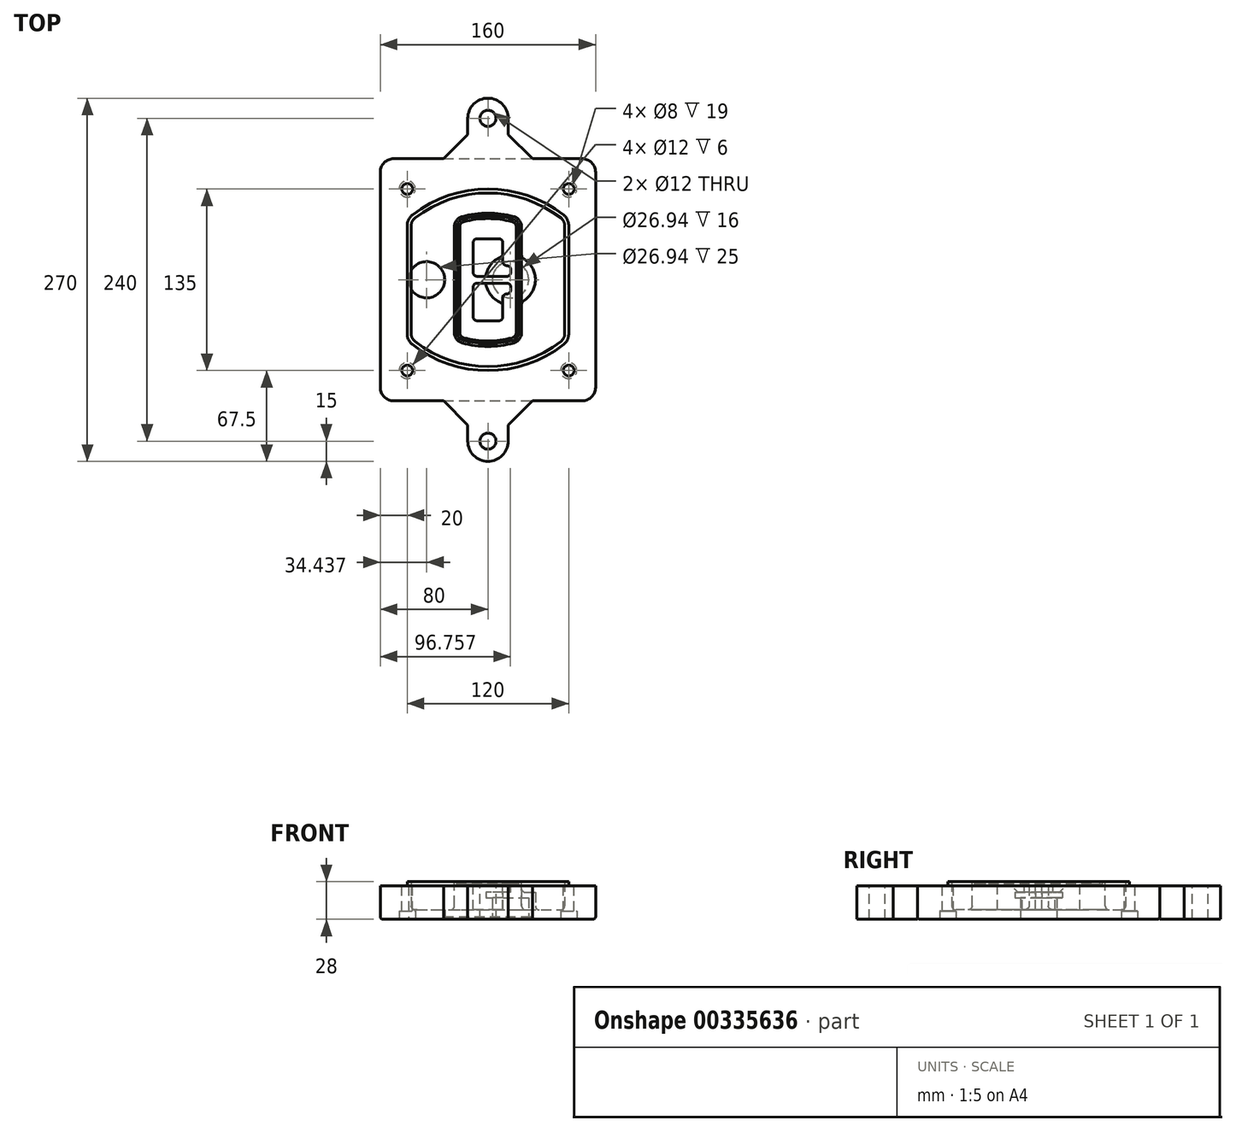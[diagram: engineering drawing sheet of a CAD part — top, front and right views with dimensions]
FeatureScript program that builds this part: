
annotation { "Feature Type Name" : "Feature", "Feature Type Description" : "" }
export const myFeature = defineFeature(function(context is Context, id is Id, definition is map)
    precondition{}
    {
        {
            var Q0;
            Q0=qCreatedBy(makeId("Top.planeOp"),FACE);
            var sketch = newSketch(context, id + "F0", { "sketchPlane" : qUnion([Q0])});
            skPoint(sketch, "E0.rect.middle", {"position": v(0, 0) * mm});
            skLineSegment(sketch, "E1.bottom", {"start": v(-70, -90) * mm, "end": v(70, -90) * mm});
            skLineSegment(sketch, "E1.top", {"start": v(-70, 90) * mm, "end": v(70, 90) * mm});
            skLineSegment(sketch, "E1.left", {"start": v(-80, -80) * mm, "end": v(-80, 80) * mm});
            skLineSegment(sketch, "E1.right", {"start": v(80, -80) * mm, "end": v(80, 80) * mm});
            skLineSegment(sketch, "E2", {"start": v(-80, 90) * mm, "end": v(80, -90) * mm, "construction": true});
            skLineSegment(sketch, "E3", {"start": v(80, 90) * mm, "end": v(-80, -90) * mm, "construction": true});
            skCircle(sketch, "E4", {"center": v(-60, 67.5) * mm, "radius": 4 * mm});
            skCircle(sketch, "E5", {"center": v(60, 67.5) * mm, "radius": 4 * mm});
            skCircle(sketch, "E6", {"center": v(60, -67.5) * mm, "radius": 4 * mm});
            skCircle(sketch, "E7", {"center": v(-60, -67.5) * mm, "radius": 4 * mm});
            skLineSegment(sketch, "E8", {"start": v(-60, 67.5) * mm, "end": v(60, 67.5) * mm, "construction": true});
            skLineSegment(sketch, "E9", {"start": v(60, 67.5) * mm, "end": v(60, -67.5) * mm, "construction": true});
            skLineSegment(sketch, "E10", {"start": v(60, -67.5) * mm, "end": v(-60, -67.5) * mm, "construction": true});
            skLineSegment(sketch, "E11", {"start": v(-60, -67.5) * mm, "end": v(-60, 67.5) * mm, "construction": true});
            skLineSegment(sketch, "E12", {"start": v(-60, 40.3) * mm, "end": v(-60, -40.3) * mm});
            skLineSegment(sketch, "E13", {"start": v(60, 40.3) * mm, "end": v(60, -40.3) * mm});
            skArc(sketch, "E14", {"start": v(56.15, 48.18) * mm, "mid": v(0, 67.5) * mm, "end": v(-56.15, 48.18) * mm});
            skArc(sketch, "E15", {"start": v(-56.15, -48.18) * mm, "mid": v(0, -67.5) * mm, "end": v(56.15, -48.18) * mm});
            skLineSegment(sketch, "E16", {"start": v(-60, 0) * mm, "end": v(60, 0) * mm, "construction": true});
            skPoint(sketch, "E17.visualSharp", {"position": v(-60, -45) * mm});
            skArc(sketch, "E17.filletArc", {"start": v(-60, -40.3) * mm, "mid": v(-58.99, -44.68) * mm, "end": v(-56.15, -48.18) * mm});
            skPoint(sketch, "E18.visualSharp", {"position": v(-60, 45) * mm});
            skArc(sketch, "E18.filletArc", {"start": v(-56.15, 48.18) * mm, "mid": v(-58.99, 44.68) * mm, "end": v(-60, 40.3) * mm});
            skPoint(sketch, "E19.visualSharp", {"position": v(60, 45) * mm});
            skArc(sketch, "E19.filletArc", {"start": v(60, 40.3) * mm, "mid": v(58.99, 44.68) * mm, "end": v(56.15, 48.18) * mm});
            skPoint(sketch, "E20.visualSharp", {"position": v(60, -45) * mm});
            skArc(sketch, "E20.filletArc", {"start": v(56.15, -48.18) * mm, "mid": v(58.99, -44.68) * mm, "end": v(60, -40.3) * mm});
            skPoint(sketch, "E21.visualSharp", {"position": v(-80, 90) * mm});
            skArc(sketch, "E21.filletArc", {"start": v(-70, 90) * mm, "mid": v(-77.07, 87.07) * mm, "end": v(-80, 80) * mm});
            skPoint(sketch, "E22.visualSharp", {"position": v(80, 90) * mm});
            skArc(sketch, "E22.filletArc", {"start": v(80, 80) * mm, "mid": v(77.07, 87.07) * mm, "end": v(70, 90) * mm});
            skPoint(sketch, "E23.visualSharp", {"position": v(80, -90) * mm});
            skArc(sketch, "E23.filletArc", {"start": v(70, -90) * mm, "mid": v(77.07, -87.07) * mm, "end": v(80, -80) * mm});
            skPoint(sketch, "E24.visualSharp", {"position": v(-80, -90) * mm});
            skArc(sketch, "E24.filletArc", {"start": v(-80, -80) * mm, "mid": v(-77.07, -87.07) * mm, "end": v(-70, -90) * mm});
            skArc(sketch, "E25.0", {"start": v(57, 40.3) * mm, "mid": v(56.3, 43.36) * mm, "end": v(54.3, 45.81) * mm});
            skLineSegment(sketch, "E25.1", {"start": v(57, 40.3) * mm, "end": v(57, -40.3) * mm});
            skArc(sketch, "E25.2", {"start": v(54.3, -45.81) * mm, "mid": v(56.3, -43.36) * mm, "end": v(57, -40.3) * mm});
            skArc(sketch, "E25.3", {"start": v(-54.3, -45.81) * mm, "mid": v(0, -64.5) * mm, "end": v(54.3, -45.81) * mm});
            skArc(sketch, "E25.4", {"start": v(-57, -40.3) * mm, "mid": v(-56.3, -43.36) * mm, "end": v(-54.3, -45.81) * mm});
            skArc(sketch, "E25.5", {"start": v(54.3, 45.81) * mm, "mid": v(0, 64.5) * mm, "end": v(-54.3, 45.81) * mm});
            skLineSegment(sketch, "E25.6", {"start": v(-57, 40.3) * mm, "end": v(-57, -40.3) * mm});
            skArc(sketch, "E25.7", {"start": v(-54.3, 45.81) * mm, "mid": v(-56.3, 43.36) * mm, "end": v(-57, 40.3) * mm});
            skArc(sketch, "E26.0", {"start": v(-58.62, 51.33) * mm, "mid": v(-62.58, 46.43) * mm, "end": v(-64, 40.3) * mm});
            skArc(sketch, "E26.1", {"start": v(58.62, 51.33) * mm, "mid": v(0, 71.5) * mm, "end": v(-58.62, 51.33) * mm});
            skArc(sketch, "E26.2", {"start": v(64, 40.3) * mm, "mid": v(62.58, 46.43) * mm, "end": v(58.62, 51.33) * mm});
            skLineSegment(sketch, "E26.3", {"start": v(64, 40.3) * mm, "end": v(64, -40.3) * mm});
            skArc(sketch, "E26.4", {"start": v(58.62, -51.33) * mm, "mid": v(62.58, -46.43) * mm, "end": v(64, -40.3) * mm});
            skLineSegment(sketch, "E26.5", {"start": v(-64, 40.3) * mm, "end": v(-64, -40.3) * mm});
            skArc(sketch, "E26.6", {"start": v(-58.62, -51.33) * mm, "mid": v(0, -71.5) * mm, "end": v(58.62, -51.33) * mm});
            skArc(sketch, "E26.7", {"start": v(-64, -40.3) * mm, "mid": v(-62.58, -46.43) * mm, "end": v(-58.62, -51.33) * mm});
            skSolve(sketch);
        }
        {
            var Q0;
            Q0=makeQuery(id+"F0.imprint","IMPRINT",FACE,{"disambiguationData":[TD([[makeQuery(id+"F0.imprint","IMPRINT",EDGE,{"derivedFrom":sQuery(id+"F0.wireOp",EDGE,"E1.bottom")}),1.0]])]});
            var Q1;
            Q1=makeQuery(id+"F0.imprint","IMPRINT",FACE,{"disambiguationData":[TD([[makeQuery(id+"F0.imprint","IMPRINT",EDGE,{"derivedFrom":sQuery(id+"F0.wireOp",EDGE,"E12")}),1.0]])]});
            var Q2;
            Q2=makeQuery(id+"F0.imprint","IMPRINT",FACE,{"disambiguationData":[TD([[makeQuery(id+"F0.imprint","IMPRINT",EDGE,{"derivedFrom":sQuery(id+"F0.wireOp",EDGE,"E25.0")}),1.0]])]});
            var Q3;
            Q3=makeQuery(id+"F0.imprint","IMPRINT",FACE,{"disambiguationData":[TD([[makeQuery(id+"F0.imprint","IMPRINT",EDGE,{"derivedFrom":sQuery(id+"F0.wireOp",EDGE,"E12")}),-1.0]])]});
            extrude(context, id + "F1", {"entities" : qUnion([Q0, Q1, Q2, Q3]), "oppositeDirection" : true, "depth" : 25 * mm});
        }
        {
            var Q0;
            Q0=makeQuery(id+"F0.imprint","IMPRINT",FACE,{"disambiguationData":[TD([[makeQuery(id+"F0.imprint","IMPRINT",EDGE,{"derivedFrom":sQuery(id+"F0.wireOp",EDGE,"E12")}),1.0]])]});
            extrude(context, id + "F2", {"entities" : qUnion([Q0]), "operationType" : NewBodyOperationType.ADD, "depth" : 3 * mm});
        }
        {
            var Q0;
            Q0=makeQuery(id+"F0.imprint","IMPRINT",FACE,{"disambiguationData":[TD([[makeQuery(id+"F0.imprint","IMPRINT",EDGE,{"derivedFrom":sQuery(id+"F0.wireOp",EDGE,"E25.0")}),1.0]])]});
            extrude(context, id + "F3", {"entities" : qUnion([Q0]), "operationType" : NewBodyOperationType.REMOVE, "oppositeDirection" : true, "depth" : 18 * mm});
        }
        {
            var Q0;
            Q0=makeQuery(id+"F2.opExtrude","CAP_FACE",FACE,{"disambiguationData":[OSD([sQuery(id+"F0.wireOp",EDGE,"E12"),sQuery(id+"F0.wireOp",EDGE,"E13"),sQuery(id+"F0.wireOp",EDGE,"E14"),sQuery(id+"F0.wireOp",EDGE,"E15"),sQuery(id+"F0.wireOp",EDGE,"E17.filletArc"),sQuery(id+"F0.wireOp",EDGE,"E18.filletArc"),sQuery(id+"F0.wireOp",EDGE,"E19.filletArc"),sQuery(id+"F0.wireOp",EDGE,"E20.filletArc"),sQuery(id+"F0.wireOp",EDGE,"E25.0"),sQuery(id+"F0.wireOp",EDGE,"E25.1"),sQuery(id+"F0.wireOp",EDGE,"E25.2"),sQuery(id+"F0.wireOp",EDGE,"E25.3"),sQuery(id+"F0.wireOp",EDGE,"E25.4"),sQuery(id+"F0.wireOp",EDGE,"E25.5"),sQuery(id+"F0.wireOp",EDGE,"E25.6"),sQuery(id+"F0.wireOp",EDGE,"E25.7")])],"isStart":false});
            var sketch = newSketch(context, id + "F4", { "sketchPlane" : qUnion([Q0])});
            skArc(sketch, "E27.0", {"start": v(-19.08, -46.97) * mm, "mid": v(0, -49.5) * mm, "end": v(19.08, -46.97) * mm});
            skArc(sketch, "E28.0", {"start": v(19.08, 46.97) * mm, "mid": v(0, 49.5) * mm, "end": v(-19.08, 46.97) * mm});
            skLineSegment(sketch, "E29", {"start": v(-25, 39.25) * mm, "end": v(-25, -39.25) * mm});
            skLineSegment(sketch, "E30", {"start": v(25, 39.25) * mm, "end": v(25, -39.25) * mm});
            skLineSegment(sketch, "E31", {"start": v(-25, 45.1) * mm, "end": v(25, 45.1) * mm, "construction": true});
            skLineSegment(sketch, "E32", {"start": v(-25, -45.1) * mm, "end": v(25, -45.1) * mm, "construction": true});
            skPoint(sketch, "E33.visualSharp", {"position": v(-25, 45.1) * mm});
            skArc(sketch, "E33.filletArc", {"start": v(-19.08, 46.97) * mm, "mid": v(-23.35, 44.11) * mm, "end": v(-25, 39.25) * mm});
            skPoint(sketch, "E34.visualSharp", {"position": v(25, 45.1) * mm});
            skArc(sketch, "E34.filletArc", {"start": v(25, 39.25) * mm, "mid": v(23.35, 44.11) * mm, "end": v(19.08, 46.97) * mm});
            skPoint(sketch, "E35.visualSharp", {"position": v(25, -45.1) * mm});
            skArc(sketch, "E35.filletArc", {"start": v(19.08, -46.97) * mm, "mid": v(23.35, -44.11) * mm, "end": v(25, -39.25) * mm});
            skPoint(sketch, "E36.visualSharp", {"position": v(-25, -45.1) * mm});
            skArc(sketch, "E36.filletArc", {"start": v(-25, -39.25) * mm, "mid": v(-23.35, -44.11) * mm, "end": v(-19.08, -46.97) * mm});
            skArc(sketch, "E37.0", {"start": v(54.3, 45.81) * mm, "mid": v(0, 64.5) * mm, "end": v(-54.3, 45.81) * mm});
            skArc(sketch, "E37.1", {"start": v(-54.3, 45.81) * mm, "mid": v(-56.3, 43.36) * mm, "end": v(-57, 40.3) * mm});
            skLineSegment(sketch, "E37.2", {"start": v(-57, 40.3) * mm, "end": v(-57, -40.3) * mm});
            skArc(sketch, "E37.3", {"start": v(-57, -40.3) * mm, "mid": v(-56.3, -43.36) * mm, "end": v(-54.3, -45.81) * mm});
            skArc(sketch, "E37.4", {"start": v(-54.3, -45.81) * mm, "mid": v(0, -64.5) * mm, "end": v(54.3, -45.81) * mm});
            skArc(sketch, "E37.5", {"start": v(54.3, -45.81) * mm, "mid": v(56.3, -43.36) * mm, "end": v(57, -40.3) * mm});
            skLineSegment(sketch, "E37.6", {"start": v(57, 40.3) * mm, "end": v(57, -40.3) * mm});
            skArc(sketch, "E37.7", {"start": v(57, 40.3) * mm, "mid": v(56.3, 43.36) * mm, "end": v(54.3, 45.81) * mm});
            skLineSegment(sketch, "E38.0", {"start": v(23, 39.25) * mm, "end": v(23, -39.25) * mm});
            skArc(sketch, "E38.1", {"start": v(18.56, -45.04) * mm, "mid": v(21.76, -42.9) * mm, "end": v(23, -39.25) * mm});
            skArc(sketch, "E38.2", {"start": v(-18.56, -45.04) * mm, "mid": v(0, -47.5) * mm, "end": v(18.56, -45.04) * mm});
            skArc(sketch, "E38.3", {"start": v(-23, -39.25) * mm, "mid": v(-21.76, -42.9) * mm, "end": v(-18.56, -45.04) * mm});
            skLineSegment(sketch, "E38.4", {"start": v(-23, 39.25) * mm, "end": v(-23, -39.25) * mm});
            skArc(sketch, "E38.5", {"start": v(23, 39.25) * mm, "mid": v(21.76, 42.9) * mm, "end": v(18.56, 45.04) * mm});
            skArc(sketch, "E38.6", {"start": v(-18.56, 45.04) * mm, "mid": v(-21.76, 42.9) * mm, "end": v(-23, 39.25) * mm});
            skArc(sketch, "E38.7", {"start": v(18.56, 45.04) * mm, "mid": v(0, 47.5) * mm, "end": v(-18.56, 45.04) * mm});
            skArc(sketch, "E39.0", {"start": v(21, 39.25) * mm, "mid": v(20.18, 41.68) * mm, "end": v(18.04, 43.1) * mm});
            skLineSegment(sketch, "E39.1", {"start": v(21, 39.25) * mm, "end": v(21, -39.25) * mm});
            skArc(sketch, "E39.2", {"start": v(18.04, -43.1) * mm, "mid": v(20.18, -41.68) * mm, "end": v(21, -39.25) * mm});
            skArc(sketch, "E39.3", {"start": v(-18.04, -43.1) * mm, "mid": v(0, -45.5) * mm, "end": v(18.04, -43.1) * mm});
            skArc(sketch, "E39.4", {"start": v(-21, -39.25) * mm, "mid": v(-20.18, -41.68) * mm, "end": v(-18.04, -43.1) * mm});
            skArc(sketch, "E39.5", {"start": v(18.04, 43.1) * mm, "mid": v(0, 45.5) * mm, "end": v(-18.04, 43.1) * mm});
            skLineSegment(sketch, "E39.6", {"start": v(-21, 39.25) * mm, "end": v(-21, -39.25) * mm});
            skArc(sketch, "E39.7", {"start": v(-18.04, 43.1) * mm, "mid": v(-20.18, 41.68) * mm, "end": v(-21, 39.25) * mm});
            skLineSegment(sketch, "E40", {"start": v(-25, 0) * mm, "end": v(25, 0) * mm, "construction": true});
            skLineSegment(sketch, "E41", {"start": v(-11, 5.5) * mm, "end": v(-11, 27.5) * mm});
            skLineSegment(sketch, "E42", {"start": v(-8, 30.5) * mm, "end": v(8, 30.5) * mm});
            skLineSegment(sketch, "E43", {"start": v(11, 27.5) * mm, "end": v(11, 13.5) * mm});
            skLineSegment(sketch, "E44", {"start": v(14, 10.5) * mm, "end": v(14, 10.5) * mm});
            skLineSegment(sketch, "E45", {"start": v(17, 7.5) * mm, "end": v(17, 5.5) * mm});
            skLineSegment(sketch, "E46", {"start": v(14, 2.5) * mm, "end": v(-8, 2.5) * mm});
            skPoint(sketch, "E47.visualSharp", {"position": v(-11, 30.5) * mm});
            skArc(sketch, "E47.filletArc", {"start": v(-8, 30.5) * mm, "mid": v(-10.12, 29.62) * mm, "end": v(-11, 27.5) * mm});
            skPoint(sketch, "E48.visualSharp", {"position": v(11, 30.5) * mm});
            skArc(sketch, "E48.filletArc", {"start": v(11, 27.5) * mm, "mid": v(10.12, 29.62) * mm, "end": v(8, 30.5) * mm});
            skPoint(sketch, "E49.visualSharp", {"position": v(11, 10.5) * mm});
            skArc(sketch, "E49.filletArc", {"start": v(11, 13.5) * mm, "mid": v(11.88, 11.38) * mm, "end": v(14, 10.5) * mm});
            skPoint(sketch, "E50.visualSharp", {"position": v(17, 10.5) * mm});
            skArc(sketch, "E50.filletArc", {"start": v(17, 7.5) * mm, "mid": v(16.12, 9.62) * mm, "end": v(14, 10.5) * mm});
            skPoint(sketch, "E51.visualSharp", {"position": v(17, 2.5) * mm});
            skArc(sketch, "E51.filletArc", {"start": v(14, 2.5) * mm, "mid": v(16.12, 3.38) * mm, "end": v(17, 5.5) * mm});
            skPoint(sketch, "E52.visualSharp", {"position": v(-11, 2.5) * mm});
            skArc(sketch, "E52.filletArc", {"start": v(-11, 5.5) * mm, "mid": v(-10.12, 3.38) * mm, "end": v(-8, 2.5) * mm});
            skLineSegment(sketch, "E53.0.MirrorCS", {"start": v(14, -2.5) * mm, "end": v(-8, -2.5) * mm});
            skArc(sketch, "E54.0.MirrorCS", {"start": v(-11, -5.5) * mm, "mid": v(-10.12, -3.38) * mm, "end": v(-8, -2.5) * mm});
            skLineSegment(sketch, "E55.0.MirrorCS", {"start": v(-11, -5.5) * mm, "end": v(-11, -27.5) * mm});
            skArc(sketch, "E56.0.MirrorCS", {"start": v(-8, -30.5) * mm, "mid": v(-10.12, -29.62) * mm, "end": v(-11, -27.5) * mm});
            skLineSegment(sketch, "E57.0.MirrorCS", {"start": v(-8, -30.5) * mm, "end": v(8, -30.5) * mm});
            skArc(sketch, "E58.0.MirrorCS", {"start": v(11, -27.5) * mm, "mid": v(10.12, -29.62) * mm, "end": v(8, -30.5) * mm});
            skLineSegment(sketch, "E59.0.MirrorCS", {"start": v(11, -27.5) * mm, "end": v(11, -13.5) * mm});
            skArc(sketch, "E60.0.MirrorCS", {"start": v(11, -13.5) * mm, "mid": v(11.88, -11.38) * mm, "end": v(14, -10.5) * mm});
            skArc(sketch, "E61.0.MirrorCS", {"start": v(17, -7.5) * mm, "mid": v(16.12, -9.62) * mm, "end": v(14, -10.5) * mm});
            skLineSegment(sketch, "E62.0.MirrorCS", {"start": v(17, -7.5) * mm, "end": v(17, -5.5) * mm});
            skArc(sketch, "E63.0.MirrorCS", {"start": v(14, -2.5) * mm, "mid": v(16.12, -3.38) * mm, "end": v(17, -5.5) * mm});
            skSolve(sketch);
        }
        {
            var Q0;
            Q0=makeQuery(id+"F4.imprint","IMPRINT",FACE,{"disambiguationData":[TD([[makeQuery(id+"F4.imprint","IMPRINT",EDGE,{"derivedFrom":sQuery(id+"F4.wireOp",EDGE,"E27.0")}),1.0]])]});
            var Q1;
            Q1=makeQuery(id+"F4.imprint","IMPRINT",FACE,{"disambiguationData":[TD([[makeQuery(id+"F4.imprint","IMPRINT",EDGE,{"derivedFrom":sQuery(id+"F4.wireOp",EDGE,"E38.0")}),-1.0]])]});
            var Q2;
            Q2=makeQuery(id+"F4.imprint","IMPRINT",FACE,{"disambiguationData":[TD([[makeQuery(id+"F4.imprint","IMPRINT",EDGE,{"derivedFrom":sQuery(id+"F4.wireOp",EDGE,"E39.0")}),1.0]])]});
            extrude(context, id + "F5", {"entities" : qUnion([Q0, Q1, Q2]), "operationType" : NewBodyOperationType.ADD, "endBound" : BoundingType.UP_TO_NEXT, "oppositeDirection" : true, "depth" : 25 * mm});
        }
        {
            var Q0;
            Q0=makeQuery(id+"F4.imprint","IMPRINT",FACE,{"disambiguationData":[TD([[makeQuery(id+"F4.imprint","IMPRINT",EDGE,{"derivedFrom":sQuery(id+"F4.wireOp",EDGE,"E38.0")}),-1.0]])]});
            extrude(context, id + "F6", {"entities" : qUnion([Q0]), "operationType" : NewBodyOperationType.REMOVE, "oppositeDirection" : true, "depth" : 2 * mm});
        }
        {
            var Q0;
            Q0=makeQuery(id+"F1.opExtrude","CAP_FACE",FACE,{"disambiguationData":[OSD([sQuery(id+"F0.wireOp",EDGE,"E1.bottom"),sQuery(id+"F0.wireOp",EDGE,"E1.top"),sQuery(id+"F0.wireOp",EDGE,"E1.left"),sQuery(id+"F0.wireOp",EDGE,"E1.right"),sQuery(id+"F0.wireOp",EDGE,"E4"),sQuery(id+"F0.wireOp",EDGE,"E5"),sQuery(id+"F0.wireOp",EDGE,"E6"),sQuery(id+"F0.wireOp",EDGE,"E7"),sQuery(id+"F0.wireOp",EDGE,"E21.filletArc"),sQuery(id+"F0.wireOp",EDGE,"E22.filletArc"),sQuery(id+"F0.wireOp",EDGE,"E23.filletArc"),sQuery(id+"F0.wireOp",EDGE,"E24.filletArc")])],"isStart":false});
            var sketch = newSketch(context, id + "F7", { "sketchPlane" : qUnion([Q0])});
            skCircle(sketch, "E64", {"center": v(16.76, 0) * mm, "radius": 13.47 * mm});
            skCircle(sketch, "E65", {"center": v(-45.56, 0) * mm, "radius": 13.47 * mm});
            skLineSegment(sketch, "E66", {"start": v(80, 0) * mm, "end": v(-80, 0) * mm});
            skCircle(sketch, "E67", {"center": v(16.76, 0) * mm, "radius": 18.47 * mm});
            skCircle(sketch, "E68", {"center": v(60, -67.5) * mm, "radius": 6 * mm});
            skCircle(sketch, "E69", {"center": v(-60, -67.5) * mm, "radius": 6 * mm});
            skCircle(sketch, "E70", {"center": v(-60, 67.5) * mm, "radius": 6 * mm});
            skCircle(sketch, "E71", {"center": v(60, 67.5) * mm, "radius": 6 * mm});
            skSolve(sketch);
        }
        {
            var Q0;
            {var subQ1=sQuery(id+"F7.wireOp",EDGE,"E66");var subQ4=sQuery(id+"F7.wireOp",EDGE,"E64");var subQ6=makeQuery(id+"F7.imprint","INTERSECT",VERTEX,{"disambiguationData":[OD(0.0)],"derivedFrom":[subQ4,subQ1]});Q0=makeQuery(id+"F7.imprint","IMPRINT",FACE,{"disambiguationData":[TD([[makeQuery(id+"F7.imprint","IMPRINT",EDGE,{"disambiguationData":[TD([[subQ6,-1.0]])],"derivedFrom":subQ4}),-1.0]])]});}
            var Q1;
            {var subQ0=sQuery(id+"F7.wireOp",EDGE,"E66");var subQ1=sQuery(id+"F7.wireOp",EDGE,"E64");var subQ3=makeQuery(id+"F7.imprint","INTERSECT",VERTEX,{"disambiguationData":[OD(0.0)],"derivedFrom":[subQ1,subQ0]});Q1=makeQuery(id+"F7.imprint","IMPRINT",FACE,{"disambiguationData":[TD([[makeQuery(id+"F7.imprint","IMPRINT",EDGE,{"disambiguationData":[TD([[subQ3,-1.0]])],"derivedFrom":subQ1}),1.0]])]});}
            var Q2;
            {var subQ0=sQuery(id+"F7.wireOp",EDGE,"E66");var subQ1=sQuery(id+"F7.wireOp",EDGE,"E64");var subQ3=makeQuery(id+"F7.imprint","INTERSECT",VERTEX,{"disambiguationData":[OD(0.0)],"derivedFrom":[subQ1,subQ0]});Q2=makeQuery(id+"F7.imprint","IMPRINT",FACE,{"disambiguationData":[TD([[makeQuery(id+"F7.imprint","IMPRINT",EDGE,{"disambiguationData":[TD([[subQ3,1.0]])],"derivedFrom":subQ1}),1.0]])]});}
            var Q3;
            {var subQ1=sQuery(id+"F7.wireOp",EDGE,"E66");var subQ4=sQuery(id+"F7.wireOp",EDGE,"E64");var subQ6=makeQuery(id+"F7.imprint","INTERSECT",VERTEX,{"disambiguationData":[OD(0.0)],"derivedFrom":[subQ4,subQ1]});Q3=makeQuery(id+"F7.imprint","IMPRINT",FACE,{"disambiguationData":[TD([[makeQuery(id+"F7.imprint","IMPRINT",EDGE,{"disambiguationData":[TD([[subQ6,1.0]])],"derivedFrom":subQ4}),-1.0]])]});}
            extrude(context, id + "F8", {"entities" : qUnion([Q0, Q1, Q2, Q3]), "operationType" : NewBodyOperationType.ADD, "oppositeDirection" : true, "depth" : 20 * mm});
        }
        {
            var Q0;
            {var subQ0=sQuery(id+"F7.wireOp",EDGE,"E66");var subQ1=sQuery(id+"F7.wireOp",EDGE,"E64");var subQ3=makeQuery(id+"F7.imprint","INTERSECT",VERTEX,{"disambiguationData":[OD(0.0)],"derivedFrom":[subQ1,subQ0]});Q0=makeQuery(id+"F7.imprint","IMPRINT",FACE,{"disambiguationData":[TD([[makeQuery(id+"F7.imprint","IMPRINT",EDGE,{"disambiguationData":[TD([[subQ3,-1.0]])],"derivedFrom":subQ1}),1.0]])]});}
            var Q1;
            {var subQ0=sQuery(id+"F7.wireOp",EDGE,"E66");var subQ1=sQuery(id+"F7.wireOp",EDGE,"E64");var subQ3=makeQuery(id+"F7.imprint","INTERSECT",VERTEX,{"disambiguationData":[OD(0.0)],"derivedFrom":[subQ1,subQ0]});Q1=makeQuery(id+"F7.imprint","IMPRINT",FACE,{"disambiguationData":[TD([[makeQuery(id+"F7.imprint","IMPRINT",EDGE,{"disambiguationData":[TD([[subQ3,1.0]])],"derivedFrom":subQ1}),1.0]])]});}
            extrude(context, id + "F9", {"entities" : qUnion([Q0, Q1]), "operationType" : NewBodyOperationType.REMOVE, "oppositeDirection" : true, "depth" : 16 * mm});
        }
        {
            var Q0;
            {var subQ0=sQuery(id+"F7.wireOp",EDGE,"E66");var subQ1=sQuery(id+"F7.wireOp",EDGE,"E65");var subQ3=makeQuery(id+"F7.imprint","INTERSECT",VERTEX,{"disambiguationData":[OD(0.0)],"derivedFrom":[subQ1,subQ0]});Q0=makeQuery(id+"F7.imprint","IMPRINT",FACE,{"disambiguationData":[TD([[makeQuery(id+"F7.imprint","IMPRINT",EDGE,{"disambiguationData":[TD([[subQ3,-1.0]])],"derivedFrom":subQ1}),1.0]])]});}
            var Q1;
            {var subQ0=sQuery(id+"F7.wireOp",EDGE,"E66");var subQ1=sQuery(id+"F7.wireOp",EDGE,"E65");var subQ3=makeQuery(id+"F7.imprint","INTERSECT",VERTEX,{"disambiguationData":[OD(0.0)],"derivedFrom":[subQ1,subQ0]});Q1=makeQuery(id+"F7.imprint","IMPRINT",FACE,{"disambiguationData":[TD([[makeQuery(id+"F7.imprint","IMPRINT",EDGE,{"disambiguationData":[TD([[subQ3,1.0]])],"derivedFrom":subQ1}),1.0]])]});}
            extrude(context, id + "F10", {"entities" : qUnion([Q0, Q1]), "operationType" : NewBodyOperationType.REMOVE, "oppositeDirection" : true, "depth" : 25 * mm});
        }
        {
            var Q0;
            Q0=makeQuery(id+"F7.imprint","IMPRINT",FACE,{"disambiguationData":[TD([[makeQuery(id+"F7.imprint","IMPRINT",EDGE,{"derivedFrom":sQuery(id+"F7.wireOp",EDGE,"E68")}),1.0]])]});
            var Q1;
            Q1=makeQuery(id+"F7.imprint","IMPRINT",FACE,{"disambiguationData":[TD([[makeQuery(id+"F7.imprint","IMPRINT",EDGE,{"derivedFrom":makeQuery(id+"F1.opExtrude","CAP_EDGE",EDGE,{"disambiguationData":[OSD([sQuery(id+"F0.wireOp",EDGE,"E5")])],"isStart":false})}),-1.0]])]});
            var Q2;
            Q2=makeQuery(id+"F7.imprint","IMPRINT",FACE,{"disambiguationData":[TD([[makeQuery(id+"F7.imprint","IMPRINT",EDGE,{"derivedFrom":sQuery(id+"F7.wireOp",EDGE,"E69")}),1.0]])]});
            var Q3;
            Q3=makeQuery(id+"F7.imprint","IMPRINT",FACE,{"disambiguationData":[TD([[makeQuery(id+"F7.imprint","IMPRINT",EDGE,{"derivedFrom":makeQuery(id+"F1.opExtrude","CAP_EDGE",EDGE,{"disambiguationData":[OSD([sQuery(id+"F0.wireOp",EDGE,"E4")])],"isStart":false})}),-1.0]])]});
            var Q4;
            Q4=makeQuery(id+"F7.imprint","IMPRINT",FACE,{"disambiguationData":[TD([[makeQuery(id+"F7.imprint","IMPRINT",EDGE,{"derivedFrom":sQuery(id+"F7.wireOp",EDGE,"E70")}),1.0]])]});
            var Q5;
            Q5=makeQuery(id+"F7.imprint","IMPRINT",FACE,{"disambiguationData":[TD([[makeQuery(id+"F7.imprint","IMPRINT",EDGE,{"derivedFrom":makeQuery(id+"F1.opExtrude","CAP_EDGE",EDGE,{"disambiguationData":[OSD([sQuery(id+"F0.wireOp",EDGE,"E7")])],"isStart":false})}),-1.0]])]});
            var Q6;
            Q6=makeQuery(id+"F7.imprint","IMPRINT",FACE,{"disambiguationData":[TD([[makeQuery(id+"F7.imprint","IMPRINT",EDGE,{"derivedFrom":sQuery(id+"F7.wireOp",EDGE,"E71")}),1.0]])]});
            var Q7;
            Q7=makeQuery(id+"F7.imprint","IMPRINT",FACE,{"disambiguationData":[TD([[makeQuery(id+"F7.imprint","IMPRINT",EDGE,{"derivedFrom":makeQuery(id+"F1.opExtrude","CAP_EDGE",EDGE,{"disambiguationData":[OSD([sQuery(id+"F0.wireOp",EDGE,"E6")])],"isStart":false})}),-1.0]])]});
            extrude(context, id + "F11", {"entities" : qUnion([Q0, Q1, Q2, Q3, Q4, Q5, Q6, Q7]), "operationType" : NewBodyOperationType.REMOVE, "oppositeDirection" : true, "depth" : 6 * mm});
        }
        {
            var Q0;
            Q0=makeQuery(id+"F9.boolean.opBoolean","COPY",FACE,{"derivedFrom":makeQuery(id+"F9.opExtrude","CAP_FACE",FACE,{"disambiguationData":[OSD([sQuery(id+"F7.wireOp",EDGE,"E64")])],"isStart":false})});
            var sketch = newSketch(context, id + "F12", { "sketchPlane" : qUnion([Q0])});
            skArc(sketch, "E72.0", {"start": v(11, 17.55) * mm, "mid": v(2.57, 11.82) * mm, "end": v(-1.54, 2.5) * mm});
            skArc(sketch, "E72.1", {"start": v(-1.54, -2.5) * mm, "mid": v(2.57, -11.82) * mm, "end": v(11, -17.55) * mm});
            skLineSegment(sketch, "E73", {"start": v(-1.54, -2.5) * mm, "end": v(14, -2.5) * mm});
            skLineSegment(sketch, "E74.0", {"start": v(14, 2.5) * mm, "end": v(-1.54, 2.5) * mm});
            skArc(sketch, "E74.1", {"start": v(14, 2.5) * mm, "mid": v(16.12, 3.38) * mm, "end": v(17, 5.5) * mm});
            skLineSegment(sketch, "E74.2", {"start": v(17, 7.5) * mm, "end": v(17, 5.5) * mm});
            skArc(sketch, "E74.3", {"start": v(17, 7.5) * mm, "mid": v(16.12, 9.62) * mm, "end": v(14, 10.5) * mm});
            skArc(sketch, "E74.4", {"start": v(11, 13.5) * mm, "mid": v(11.88, 11.38) * mm, "end": v(14, 10.5) * mm});
            skLineSegment(sketch, "E74.5", {"start": v(11, 17.55) * mm, "end": v(11, 13.5) * mm});
            skLineSegment(sketch, "E74.7", {"start": v(14, -2.5) * mm, "end": v(-1.54, -2.5) * mm});
            skArc(sketch, "E74.8", {"start": v(14, -2.5) * mm, "mid": v(16.12, -3.38) * mm, "end": v(17, -5.5) * mm});
            skLineSegment(sketch, "E74.9", {"start": v(17, -7.5) * mm, "end": v(17, -5.5) * mm});
            skArc(sketch, "E74.10", {"start": v(17, -7.5) * mm, "mid": v(16.12, -9.62) * mm, "end": v(14, -10.5) * mm});
            skArc(sketch, "E74.11", {"start": v(11, -13.5) * mm, "mid": v(11.88, -11.38) * mm, "end": v(14, -10.5) * mm});
            skLineSegment(sketch, "E74.12", {"start": v(11, -17.55) * mm, "end": v(11, -13.5) * mm});
            skPoint(sketch, "E75.orphan", {"position": v(11, -27.5) * mm});
            skPoint(sketch, "E76.orphan", {"position": v(-8, -2.5) * mm});
            skPoint(sketch, "E77.orphan", {"position": v(-8, 2.5) * mm});
            skPoint(sketch, "E78.orphan", {"position": v(11, 27.5) * mm});
            skSolve(sketch);
        }
        {
            var Q0;
            {var subQ7=sQuery(id+"F12.wireOp",EDGE,"E72.0");var subQ14=sQuery(id+"F12.wireOp",EDGE,"E72.1");var subQ16=sQuery(id+"F12.wireOp",EDGE,"E74.1");var subQ18=sQuery(id+"F12.wireOp",EDGE,"E74.8");Q0=qUnion([makeQuery(id+"F12.imprint","IMPRINT",FACE,{"disambiguationData":[TD([[makeQuery(id+"F12.imprint","IMPRINT",EDGE,{"derivedFrom":subQ7}),1.0]])]}),makeQuery(id+"F12.imprint","IMPRINT",FACE,{"disambiguationData":[TD([[makeQuery(id+"F12.imprint","IMPRINT",EDGE,{"derivedFrom":subQ14}),1.0]])]}),makeQuery(id+"F12.imprint","IMPRINT",FACE,{"disambiguationData":[TD([[makeQuery(id+"F12.imprint","IMPRINT",EDGE,{"derivedFrom":subQ16}),1.0]])]}),makeQuery(id+"F12.imprint","IMPRINT",FACE,{"disambiguationData":[TD([[makeQuery(id+"F12.imprint","IMPRINT",EDGE,{"derivedFrom":subQ18}),-1.0]])]})]);}
            var Q1;
            Q1=makeQuery(id+"F5.boolean.opBoolean","SPLIT",FACE,{"disambiguationData":[TD([makeQuery(id+"F5.opExtrude","SWEPT_FACE",FACE,{"disambiguationData":[OSD([sQuery(id+"F4.wireOp",EDGE,"E41")])]})])],"derivedFrom":makeQuery(id+"F3.boolean.opBoolean","COPY",FACE,{"derivedFrom":makeQuery(id+"F3.opExtrude","CAP_FACE",FACE,{"disambiguationData":[OSD([sQuery(id+"F0.wireOp",EDGE,"E25.0"),sQuery(id+"F0.wireOp",EDGE,"E25.1"),sQuery(id+"F0.wireOp",EDGE,"E25.2"),sQuery(id+"F0.wireOp",EDGE,"E25.3"),sQuery(id+"F0.wireOp",EDGE,"E25.4"),sQuery(id+"F0.wireOp",EDGE,"E25.5"),sQuery(id+"F0.wireOp",EDGE,"E25.6"),sQuery(id+"F0.wireOp",EDGE,"E25.7")])],"isStart":false})})});
            extrude(context, id + "F13", {"entities" : qUnion([Q0]), "operationType" : NewBodyOperationType.REMOVE, "endBound" : BoundingType.UP_TO_SURFACE, "endBoundEntityFace" : qUnion([Q1]), "depth" : 25 * mm});
        }
        {
            var Q0;
            Q0=makeQuery(id+"F3.boolean.opBoolean","COPY",EDGE,{"derivedFrom":makeQuery(id+"F3.opExtrude","CAP_EDGE",EDGE,{"disambiguationData":[OSD([sQuery(id+"F0.wireOp",EDGE,"E25.6")])],"isStart":false})});
            var Q1;
            Q1=makeQuery(id+"F8.boolean.opBoolean","INTERSECT",EDGE,{"derivedFrom":[makeQuery(id+"F5.opExtrude","SWEPT_FACE",FACE,{"disambiguationData":[OSD([sQuery(id+"F4.wireOp",EDGE,"E30")])]}),makeQuery(id+"F8.opExtrude","CAP_FACE",FACE,{"disambiguationData":[OSD([sQuery(id+"F7.wireOp",EDGE,"E67")])],"isStart":false})]});
            var Q2;
            Q2=makeQuery(id+"F8.boolean.opBoolean","INTERSECT",EDGE,{"disambiguationData":[OD(1.0)],"derivedFrom":[makeQuery(id+"F5.opExtrude","SWEPT_FACE",FACE,{"disambiguationData":[OSD([sQuery(id+"F4.wireOp",EDGE,"E30")])]}),makeQuery(id+"F8.opExtrude","SWEPT_FACE",FACE,{"disambiguationData":[OSD([sQuery(id+"F7.wireOp",EDGE,"E67")])]})]});
            var Q3;
            {var subQ0=sQuery(id+"F4.wireOp",EDGE,"E30");Q3=makeQuery(id+"F8.boolean.opBoolean","SPLIT",EDGE,{"disambiguationData":[TD([makeQuery(id+"F5.opExtrude","SWEPT_FACE",FACE,{"disambiguationData":[OSD([sQuery(id+"F4.wireOp",EDGE,"E35.filletArc")])]})])],"derivedFrom":makeQuery(id+"F5.opExtrude","CAP_EDGE",EDGE,{"disambiguationData":[OSD([subQ0])],"isStart":false})});}
            var Q4;
            {var subQ0=sQuery(id+"F0.wireOp",EDGE,"E25.7");var subQ1=sQuery(id+"F0.wireOp",EDGE,"E25.1");var subQ2=sQuery(id+"F0.wireOp",EDGE,"E25.6");var subQ3=sQuery(id+"F0.wireOp",EDGE,"E25.5");var subQ4=sQuery(id+"F0.wireOp",EDGE,"E25.4");var subQ5=sQuery(id+"F0.wireOp",EDGE,"E25.0");var subQ6=sQuery(id+"F0.wireOp",EDGE,"E25.2");var subQ7=sQuery(id+"F0.wireOp",EDGE,"E25.3");Q4=makeQuery(id+"F8.boolean.opBoolean","INTERSECT",EDGE,{"derivedFrom":[makeQuery(id+"F5.boolean.opBoolean","SPLIT",FACE,{"disambiguationData":[TD([makeQuery(id+"F2.opExtrude","SWEPT_FACE",FACE,{"disambiguationData":[OSD([subQ5])]})])],"derivedFrom":makeQuery(id+"F3.boolean.opBoolean","COPY",FACE,{"derivedFrom":makeQuery(id+"F3.opExtrude","CAP_FACE",FACE,{"disambiguationData":[OSD([subQ5,subQ1,subQ6,subQ7,subQ4,subQ3,subQ2,subQ0])],"isStart":false})})}),makeQuery(id+"F8.opExtrude","SWEPT_FACE",FACE,{"disambiguationData":[OSD([sQuery(id+"F7.wireOp",EDGE,"E67")])]})]});}
            var Q5;
            Q5=makeQuery(id+"F8.boolean.opBoolean","INTERSECT",EDGE,{"disambiguationData":[OD(0.0)],"derivedFrom":[makeQuery(id+"F5.opExtrude","SWEPT_FACE",FACE,{"disambiguationData":[OSD([sQuery(id+"F4.wireOp",EDGE,"E30")])]}),makeQuery(id+"F8.opExtrude","SWEPT_FACE",FACE,{"disambiguationData":[OSD([sQuery(id+"F7.wireOp",EDGE,"E67")])]})]});
            fillet(context, id + "F14", {"entities" : qUnion([Q0, Q1, Q2, Q3, Q4, Q5]), "radius" : 3 * mm, "tangentPropagation" : true, "allowEdgeOverflow" : false});
        }
        {
            var Q0;
            Q0=makeQuery(id+"F1.opExtrude","CAP_EDGE",EDGE,{"disambiguationData":[OSD([sQuery(id+"F0.wireOp",EDGE,"E1.bottom")])],"isStart":false});
            fillet(context, id + "F15", {"entities" : qUnion([Q0]), "radius" : 2 * mm, "tangentPropagation" : true, "allowEdgeOverflow" : false});
        }
        {
            var Q0;
            {var subQ0=sQuery(id+"F0.wireOp",EDGE,"E21.filletArc");var subQ1=sQuery(id+"F0.wireOp",EDGE,"E7");var subQ2=sQuery(id+"F0.wireOp",EDGE,"E6");var subQ3=sQuery(id+"F0.wireOp",EDGE,"E5");var subQ4=sQuery(id+"F0.wireOp",EDGE,"E4");var subQ5=sQuery(id+"F0.wireOp",EDGE,"E22.filletArc");var subQ6=sQuery(id+"F0.wireOp",EDGE,"E1.bottom");var subQ7=sQuery(id+"F0.wireOp",EDGE,"E1.right");var subQ8=sQuery(id+"F0.wireOp",EDGE,"E1.top");var subQ9=sQuery(id+"F0.wireOp",EDGE,"E1.left");var subQ10=sQuery(id+"F0.wireOp",EDGE,"E23.filletArc");var subQ11=sQuery(id+"F0.wireOp",EDGE,"E24.filletArc");Q0=makeQuery(id+"F2.boolean.opBoolean","SPLIT",FACE,{"disambiguationData":[TD([makeQuery(id+"F1.opExtrude","SWEPT_FACE",FACE,{"disambiguationData":[OSD([subQ6])]})])],"derivedFrom":makeQuery(id+"F1.opExtrude","CAP_FACE",FACE,{"disambiguationData":[OSD([subQ6,subQ8,subQ9,subQ7,subQ4,subQ3,subQ2,subQ1,subQ0,subQ5,subQ10,subQ11])],"isStart":true})});}
            var sketch = newSketch(context, id + "F16", { "sketchPlane" : qUnion([Q0])});
            skLineSegment(sketch, "E79", {"start": v(0, 90) * mm, "end": v(0, 120) * mm, "construction": true});
            skCircle(sketch, "E80", {"center": v(0, 120) * mm, "radius": 6 * mm});
            skLineSegment(sketch, "E81", {"start": v(-33, 90) * mm, "end": v(-15, 108) * mm});
            skLineSegment(sketch, "E82", {"start": v(-15, 108) * mm, "end": v(-15, 120) * mm});
            skLineSegment(sketch, "E83", {"start": v(15, 108) * mm, "end": v(33, 90) * mm});
            skLineSegment(sketch, "E84", {"start": v(33, 90) * mm, "end": v(15, 108) * mm});
            skLineSegment(sketch, "E85", {"start": v(15, 108) * mm, "end": v(15, 120) * mm});
            skArc(sketch, "E86", {"start": v(15, 120) * mm, "mid": v(0, 135) * mm, "end": v(-15, 120) * mm});
            skLineSegment(sketch, "E87", {"start": v(0, -90) * mm, "end": v(0, -120) * mm, "construction": true});
            skLineSegment(sketch, "E88", {"start": v(33, -90) * mm, "end": v(15, -108) * mm});
            skLineSegment(sketch, "E89", {"start": v(15, -108) * mm, "end": v(15, -120) * mm});
            skLineSegment(sketch, "E90", {"start": v(-15, -108) * mm, "end": v(-33, -90) * mm});
            skLineSegment(sketch, "E91", {"start": v(-15, -108) * mm, "end": v(-15, -120) * mm});
            skCircle(sketch, "E92", {"center": v(0, -120) * mm, "radius": 6 * mm});
            skArc(sketch, "E93", {"start": v(-15, -120) * mm, "mid": v(0, -135) * mm, "end": v(15, -120) * mm});
            skSolve(sketch);
        }
        {
            var Q0;
            {var subQ1=sQuery(id+"F16.wireOp",EDGE,"E88");Q0=makeQuery(id+"F16.imprint","IMPRINT",FACE,{"disambiguationData":[TD([[makeQuery(id+"F16.imprint","IMPRINT",EDGE,{"derivedFrom":subQ1}),-1.0]])]});}
            var Q1;
            Q1=makeQuery(id+"F16.imprint","IMPRINT",FACE,{"disambiguationData":[TD([[makeQuery(id+"F16.imprint","IMPRINT",EDGE,{"derivedFrom":sQuery(id+"F16.wireOp",EDGE,"E80")}),-1.0]])]});
            extrude(context, id + "F17", {"entities" : qUnion([Q0, Q1]), "operationType" : NewBodyOperationType.ADD, "depth" : -25 * mm});
        }
    });
